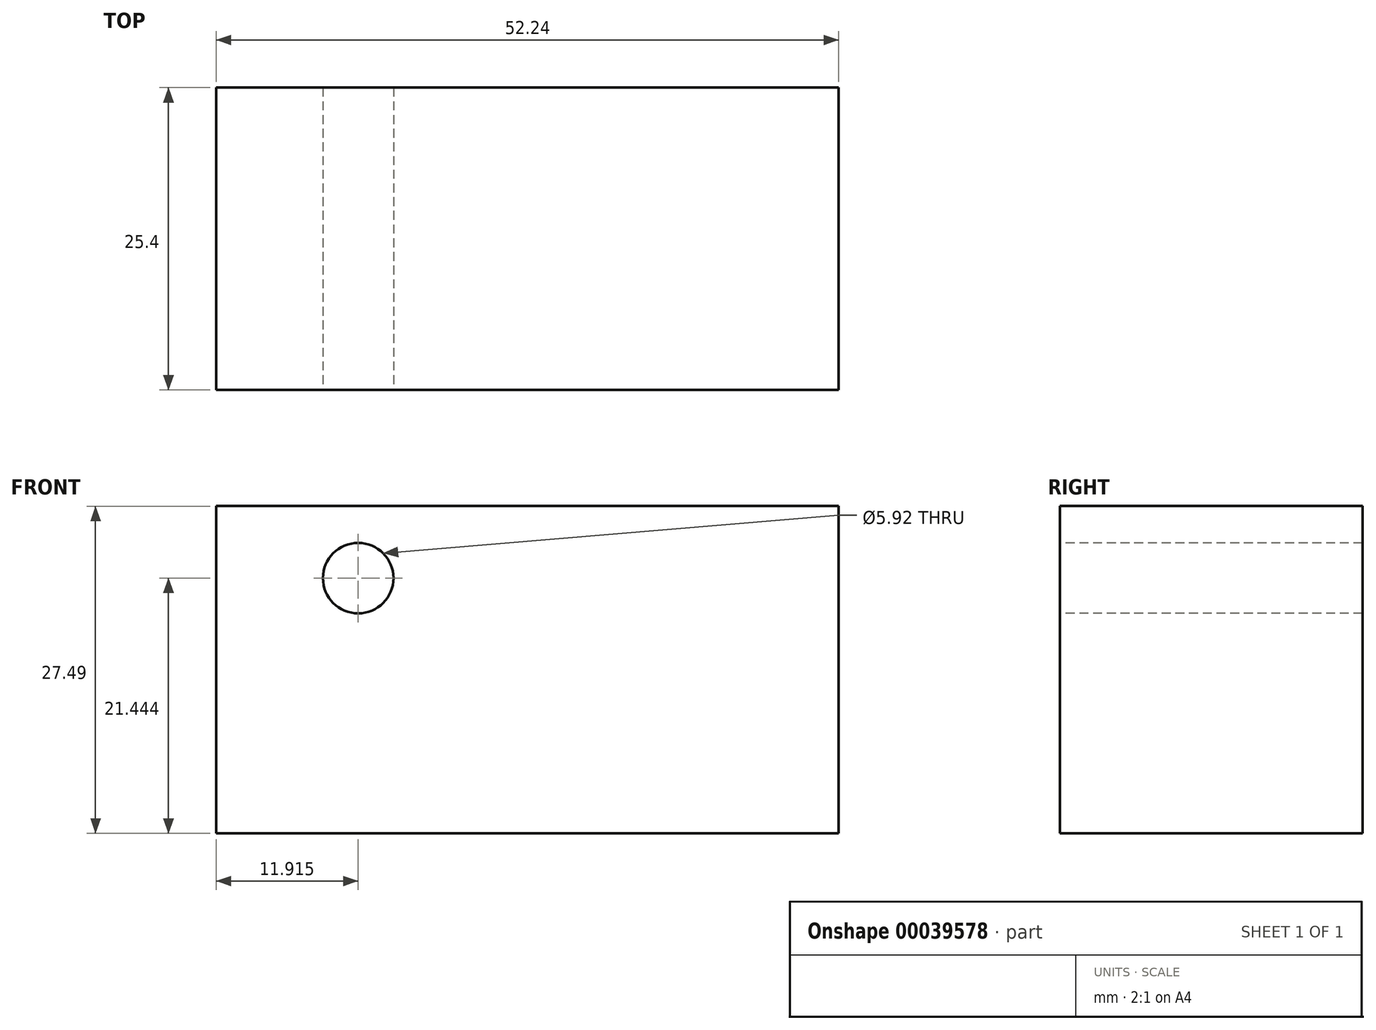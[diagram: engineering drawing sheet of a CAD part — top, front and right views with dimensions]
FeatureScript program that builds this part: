
annotation { "Feature Type Name" : "Feature", "Feature Type Description" : "" }
export const myFeature = defineFeature(function(context is Context, id is Id, definition is map)
    precondition{}
    {
        {
            var Q0;
            Q0=qCreatedBy(makeId("Front.planeOp"),FACE);
            var sketch = newSketch(context, id + "F0", { "sketchPlane" : qUnion([Q0])});
            skLineSegment(sketch, "E0.bottom", {"start": v(-42.16, 31.25) * mm, "end": v(10.08, 31.25) * mm});
            skLineSegment(sketch, "E0.top", {"start": v(-42.16, 3.76) * mm, "end": v(10.08, 3.76) * mm});
            skLineSegment(sketch, "E0.left", {"start": v(-42.16, 31.25) * mm, "end": v(-42.16, 3.76) * mm});
            skLineSegment(sketch, "E0.right", {"start": v(10.08, 31.25) * mm, "end": v(10.08, 3.76) * mm});
            skSolve(sketch);
        }
        {
            var Q0;
            Q0=makeQuery(id+"F0.imprint","IMPRINT",FACE,{"disambiguationData":[TD([[makeQuery(id+"F0.imprint","IMPRINT",EDGE,{"derivedFrom":sQuery(id+"F0.wireOp",EDGE,"E0.bottom")}),-1.0]])]});
            extrude(context, id + "F1", {"entities" : qUnion([Q0]), "depth" : 25.4 * mm});
        }
        {
            var Q0;
            Q0=makeQuery(id+"F1.opExtrude","CAP_FACE",FACE,{"disambiguationData":[OSD([sQuery(id+"F0.wireOp",EDGE,"E0.bottom"),sQuery(id+"F0.wireOp",EDGE,"E0.top"),sQuery(id+"F0.wireOp",EDGE,"E0.left"),sQuery(id+"F0.wireOp",EDGE,"E0.right")])],"isStart":false});
            var sketch = newSketch(context, id + "F2", { "sketchPlane" : qUnion([Q0])});
            skCircle(sketch, "E1", {"center": v(-30.24, 25.2) * mm, "radius": 2.96 * mm});
            skSolve(sketch);
        }
        {
            var Q0;
            Q0=makeQuery(id+"F2.imprint","IMPRINT",FACE,{"disambiguationData":[TD([[makeQuery(id+"F2.imprint","IMPRINT",EDGE,{"derivedFrom":sQuery(id+"F2.wireOp",EDGE,"E1")}),1.0]])]});
            extrude(context, id + "F3", {"entities" : qUnion([Q0]), "operationType" : NewBodyOperationType.REMOVE, "endBound" : BoundingType.THROUGH_ALL, "oppositeDirection" : true, "depth" : 25.4 * mm});
        }
    });
